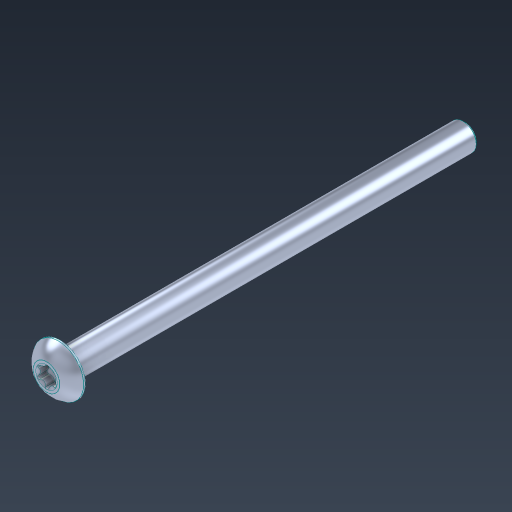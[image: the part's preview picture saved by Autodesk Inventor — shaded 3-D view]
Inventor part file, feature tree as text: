
AUTODESK INVENTOR PART (.ipt)
format: ipt  version: 2024.3 (Build 283343000, 343)  size: 160,768 bytes
history: native  units: in
note: dims shown in document units (in); Inventor stores cm internally (conversion verified against a paired STEP export)
features: fillet x1
ambient origin geometry x8: Origin, YZ Plane, XZ Plane, XY Plane, X Axis, Y Axis, Z Axis, Center Point
bodies: Solid1 (feature_tree)
feature tree (1):
  fillet  "Fillet1"  [1 undecoded]
note: 1 required parameter value undecoded (feature->parameter linkage not recoverable at this tier; creation-order binding heuristic only, values carry confidence <= 0.55)
